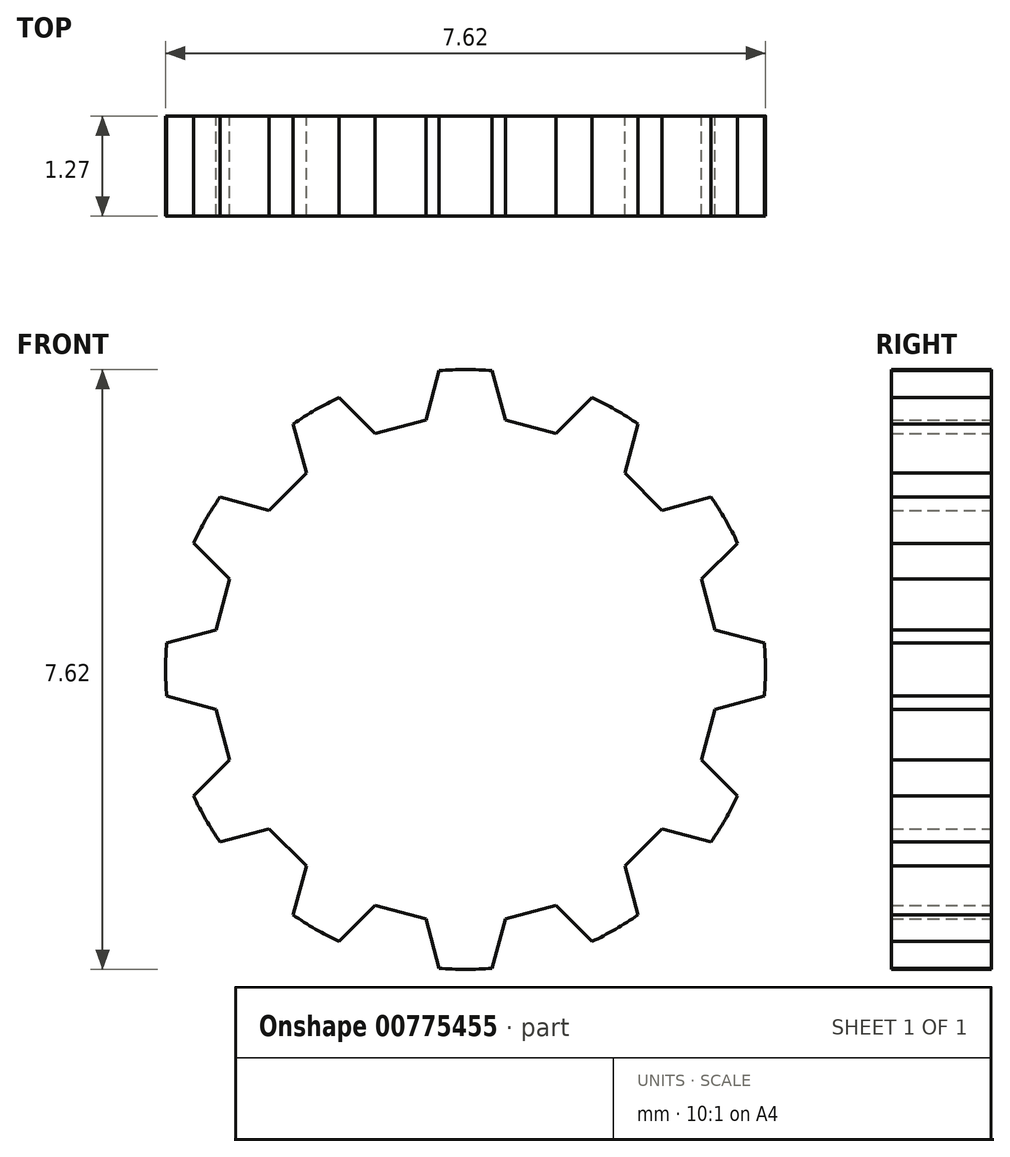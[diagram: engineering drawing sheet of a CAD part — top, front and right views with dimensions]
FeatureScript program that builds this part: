
annotation { "Feature Type Name" : "Feature", "Feature Type Description" : "" }
export const myFeature = defineFeature(function(context is Context, id is Id, definition is map)
    precondition{}
    {
        {
            var Q0;
            Q0=qCreatedBy(makeId("Front.planeOp"),FACE);
            var sketch = newSketch(context, id + "F0", { "sketchPlane" : qUnion([Q0])});
            skCircle(sketch, "E0", {"center": v(0, 0) * mm, "radius": 3.81 * mm});
            skLineSegment(sketch, "E1", {"start": v(0, 0) * mm, "end": v(3.81, 0) * mm});
            skLineSegment(sketch, "E2", {"start": v(3.81, 0) * mm, "end": v(3.81, 0.33) * mm});
            skLineSegment(sketch, "E3", {"start": v(3.81, 0) * mm, "end": v(3.81, -0.33) * mm});
            skLineSegment(sketch, "E4", {"start": v(3.81, 0.33) * mm, "end": v(0, 0) * mm});
            skLineSegment(sketch, "E5", {"start": v(0, 0) * mm, "end": v(4.96, 1.33) * mm});
            skLineSegment(sketch, "E6", {"start": v(3.08, 0.83) * mm, "end": v(3.17, 0.5) * mm});
            skLineSegment(sketch, "E7", {"start": v(3.08, 0.83) * mm, "end": v(3, 1.15) * mm});
            skLineSegment(sketch, "E8", {"start": v(3.17, 0.5) * mm, "end": v(3.8, 0.33) * mm});
            skLineSegment(sketch, "E9", {"start": v(3, 1.15) * mm, "end": v(3.47, 1.62) * mm});
            skLineSegment(sketch, "E10", {"start": v(3.47, 1.62) * mm, "end": v(3.8, 0.33) * mm});
            skLineSegment(sketch, "E11.1.0", {"start": v(2.02, 2.5) * mm, "end": v(2.2, 3.14) * mm});
            skLineSegment(sketch, "E11.1.1", {"start": v(2.2, 3.14) * mm, "end": v(3.13, 2.2) * mm});
            skLineSegment(sketch, "E11.1.2", {"start": v(2.26, 2.26) * mm, "end": v(2.5, 2.02) * mm});
            skLineSegment(sketch, "E11.1.3", {"start": v(2.26, 2.26) * mm, "end": v(2.02, 2.5) * mm});
            skLineSegment(sketch, "E11.1.4", {"start": v(2.5, 2.02) * mm, "end": v(3.13, 2.2) * mm});
            skLineSegment(sketch, "E11.1.5", {"start": v(3.3, 1.9) * mm, "end": v(3.47, 1.62) * mm});
            skLineSegment(sketch, "E11.1.6", {"start": v(3.3, 1.9) * mm, "end": v(3.13, 2.2) * mm});
            skLineSegment(sketch, "E11.2.0", {"start": v(0.5, 3.17) * mm, "end": v(0.33, 3.82) * mm});
            skLineSegment(sketch, "E11.2.1", {"start": v(0.33, 3.82) * mm, "end": v(1.62, 3.47) * mm});
            skLineSegment(sketch, "E11.2.2", {"start": v(0.83, 3.08) * mm, "end": v(1.15, 3) * mm});
            skLineSegment(sketch, "E11.2.3", {"start": v(0.83, 3.08) * mm, "end": v(0.5, 3.17) * mm});
            skLineSegment(sketch, "E11.2.4", {"start": v(1.15, 3) * mm, "end": v(1.62, 3.47) * mm});
            skLineSegment(sketch, "E11.2.5", {"start": v(1.9, 3.3) * mm, "end": v(2.2, 3.13) * mm});
            skLineSegment(sketch, "E11.2.6", {"start": v(1.9, 3.3) * mm, "end": v(1.62, 3.47) * mm});
            skLineSegment(sketch, "E11.3.0", {"start": v(-1.15, 3) * mm, "end": v(-1.62, 3.47) * mm});
            skLineSegment(sketch, "E11.3.1", {"start": v(-1.62, 3.47) * mm, "end": v(-0.33, 3.8) * mm});
            skLineSegment(sketch, "E11.3.2", {"start": v(-0.83, 3.08) * mm, "end": v(-0.5, 3.17) * mm});
            skLineSegment(sketch, "E11.3.3", {"start": v(-0.83, 3.08) * mm, "end": v(-1.15, 3) * mm});
            skLineSegment(sketch, "E11.3.4", {"start": v(-0.5, 3.17) * mm, "end": v(-0.33, 3.8) * mm});
            skLineSegment(sketch, "E11.3.5", {"start": v(0, 3.81) * mm, "end": v(0.33, 3.81) * mm});
            skLineSegment(sketch, "E11.3.6", {"start": v(0, 3.81) * mm, "end": v(-0.33, 3.81) * mm});
            skLineSegment(sketch, "E11.4.0", {"start": v(-2.5, 2.02) * mm, "end": v(-3.14, 2.2) * mm});
            skLineSegment(sketch, "E11.4.1", {"start": v(-3.14, 2.2) * mm, "end": v(-2.2, 3.13) * mm});
            skLineSegment(sketch, "E11.4.2", {"start": v(-2.26, 2.26) * mm, "end": v(-2.02, 2.5) * mm});
            skLineSegment(sketch, "E11.4.3", {"start": v(-2.26, 2.26) * mm, "end": v(-2.5, 2.02) * mm});
            skLineSegment(sketch, "E11.4.4", {"start": v(-2.02, 2.5) * mm, "end": v(-2.2, 3.13) * mm});
            skLineSegment(sketch, "E11.4.5", {"start": v(-1.9, 3.3) * mm, "end": v(-1.62, 3.47) * mm});
            skLineSegment(sketch, "E11.4.6", {"start": v(-1.9, 3.3) * mm, "end": v(-2.2, 3.13) * mm});
            skLineSegment(sketch, "E11.5.0", {"start": v(-3.17, 0.5) * mm, "end": v(-3.82, 0.33) * mm});
            skLineSegment(sketch, "E11.5.1", {"start": v(-3.82, 0.33) * mm, "end": v(-3.47, 1.62) * mm});
            skLineSegment(sketch, "E11.5.2", {"start": v(-3.08, 0.83) * mm, "end": v(-3, 1.15) * mm});
            skLineSegment(sketch, "E11.5.3", {"start": v(-3.08, 0.83) * mm, "end": v(-3.17, 0.5) * mm});
            skLineSegment(sketch, "E11.5.4", {"start": v(-3, 1.15) * mm, "end": v(-3.47, 1.62) * mm});
            skLineSegment(sketch, "E11.5.5", {"start": v(-3.3, 1.9) * mm, "end": v(-3.13, 2.2) * mm});
            skLineSegment(sketch, "E11.5.6", {"start": v(-3.3, 1.9) * mm, "end": v(-3.47, 1.62) * mm});
            skLineSegment(sketch, "E11.6.0", {"start": v(-3, -1.15) * mm, "end": v(-3.47, -1.62) * mm});
            skLineSegment(sketch, "E11.6.1", {"start": v(-3.47, -1.62) * mm, "end": v(-3.8, -0.33) * mm});
            skLineSegment(sketch, "E11.6.2", {"start": v(-3.08, -0.83) * mm, "end": v(-3.17, -0.5) * mm});
            skLineSegment(sketch, "E11.6.3", {"start": v(-3.08, -0.83) * mm, "end": v(-3, -1.15) * mm});
            skLineSegment(sketch, "E11.6.4", {"start": v(-3.17, -0.5) * mm, "end": v(-3.8, -0.33) * mm});
            skLineSegment(sketch, "E11.6.5", {"start": v(-3.81, 0) * mm, "end": v(-3.81, 0.33) * mm});
            skLineSegment(sketch, "E11.6.6", {"start": v(-3.81, 0) * mm, "end": v(-3.81, -0.33) * mm});
            skLineSegment(sketch, "E11.7.0", {"start": v(-2.02, -2.5) * mm, "end": v(-2.2, -3.14) * mm});
            skLineSegment(sketch, "E11.7.1", {"start": v(-2.2, -3.14) * mm, "end": v(-3.13, -2.2) * mm});
            skLineSegment(sketch, "E11.7.2", {"start": v(-2.26, -2.26) * mm, "end": v(-2.5, -2.02) * mm});
            skLineSegment(sketch, "E11.7.3", {"start": v(-2.26, -2.26) * mm, "end": v(-2.02, -2.5) * mm});
            skLineSegment(sketch, "E11.7.4", {"start": v(-2.5, -2.02) * mm, "end": v(-3.13, -2.2) * mm});
            skLineSegment(sketch, "E11.7.5", {"start": v(-3.3, -1.9) * mm, "end": v(-3.47, -1.62) * mm});
            skLineSegment(sketch, "E11.7.6", {"start": v(-3.3, -1.9) * mm, "end": v(-3.13, -2.2) * mm});
            skLineSegment(sketch, "E11.8.0", {"start": v(-0.5, -3.17) * mm, "end": v(-0.33, -3.82) * mm});
            skLineSegment(sketch, "E11.8.1", {"start": v(-0.33, -3.82) * mm, "end": v(-1.62, -3.47) * mm});
            skLineSegment(sketch, "E11.8.2", {"start": v(-0.83, -3.08) * mm, "end": v(-1.15, -3) * mm});
            skLineSegment(sketch, "E11.8.3", {"start": v(-0.83, -3.08) * mm, "end": v(-0.5, -3.17) * mm});
            skLineSegment(sketch, "E11.8.4", {"start": v(-1.15, -3) * mm, "end": v(-1.62, -3.47) * mm});
            skLineSegment(sketch, "E11.8.5", {"start": v(-1.9, -3.3) * mm, "end": v(-2.2, -3.13) * mm});
            skLineSegment(sketch, "E11.8.6", {"start": v(-1.9, -3.3) * mm, "end": v(-1.62, -3.47) * mm});
            skLineSegment(sketch, "E11.9.0", {"start": v(1.15, -3) * mm, "end": v(1.62, -3.47) * mm});
            skLineSegment(sketch, "E11.9.1", {"start": v(1.62, -3.47) * mm, "end": v(0.33, -3.8) * mm});
            skLineSegment(sketch, "E11.9.2", {"start": v(0.83, -3.08) * mm, "end": v(0.5, -3.17) * mm});
            skLineSegment(sketch, "E11.9.3", {"start": v(0.83, -3.08) * mm, "end": v(1.15, -3) * mm});
            skLineSegment(sketch, "E11.9.4", {"start": v(0.5, -3.17) * mm, "end": v(0.33, -3.8) * mm});
            skLineSegment(sketch, "E11.9.5", {"start": v(0, -3.81) * mm, "end": v(-0.33, -3.81) * mm});
            skLineSegment(sketch, "E11.9.6", {"start": v(0, -3.81) * mm, "end": v(0.33, -3.81) * mm});
            skLineSegment(sketch, "E11.10.0", {"start": v(2.5, -2.02) * mm, "end": v(3.14, -2.2) * mm});
            skLineSegment(sketch, "E11.10.1", {"start": v(3.14, -2.2) * mm, "end": v(2.2, -3.13) * mm});
            skLineSegment(sketch, "E11.10.2", {"start": v(2.26, -2.26) * mm, "end": v(2.02, -2.5) * mm});
            skLineSegment(sketch, "E11.10.3", {"start": v(2.26, -2.26) * mm, "end": v(2.5, -2.02) * mm});
            skLineSegment(sketch, "E11.10.4", {"start": v(2.02, -2.5) * mm, "end": v(2.2, -3.13) * mm});
            skLineSegment(sketch, "E11.10.5", {"start": v(1.9, -3.3) * mm, "end": v(1.62, -3.47) * mm});
            skLineSegment(sketch, "E11.10.6", {"start": v(1.9, -3.3) * mm, "end": v(2.2, -3.13) * mm});
            skLineSegment(sketch, "E11.11.0", {"start": v(3.17, -0.5) * mm, "end": v(3.82, -0.33) * mm});
            skLineSegment(sketch, "E11.11.1", {"start": v(3.82, -0.33) * mm, "end": v(3.47, -1.62) * mm});
            skLineSegment(sketch, "E11.11.2", {"start": v(3.08, -0.83) * mm, "end": v(3, -1.15) * mm});
            skLineSegment(sketch, "E11.11.3", {"start": v(3.08, -0.83) * mm, "end": v(3.17, -0.5) * mm});
            skLineSegment(sketch, "E11.11.4", {"start": v(3, -1.15) * mm, "end": v(3.47, -1.62) * mm});
            skLineSegment(sketch, "E11.11.5", {"start": v(3.3, -1.9) * mm, "end": v(3.13, -2.2) * mm});
            skLineSegment(sketch, "E11.11.6", {"start": v(3.3, -1.9) * mm, "end": v(3.47, -1.62) * mm});
            skSolve(sketch);
        }
        {
            var Q0;
            {var subQ25=sQuery(id+"F0.wireOp",EDGE,"E1");Q0=makeQuery(id+"F0.imprint","IMPRINT",FACE,{"disambiguationData":[TD([[makeQuery(id+"F0.imprint","IMPRINT",EDGE,{"derivedFrom":subQ25}),-1.0]])]});}
            var Q1;
            {var subQ0=sQuery(id+"F0.wireOp",EDGE,"E6");Q1=makeQuery(id+"F0.imprint","IMPRINT",FACE,{"disambiguationData":[TD([[makeQuery(id+"F0.imprint","IMPRINT",EDGE,{"derivedFrom":subQ0}),-1.0]])]});}
            var Q2;
            {var subQ0=sQuery(id+"F0.wireOp",EDGE,"E1");Q2=makeQuery(id+"F0.imprint","IMPRINT",FACE,{"disambiguationData":[TD([[makeQuery(id+"F0.imprint","IMPRINT",EDGE,{"derivedFrom":subQ0}),1.0]])]});}
            extrude(context, id + "F1", {"entities" : qUnion([Q0, Q1, Q2]), "depth" : 1.27 * mm, "offsetDistance" : 25.4 * mm});
        }
    });
